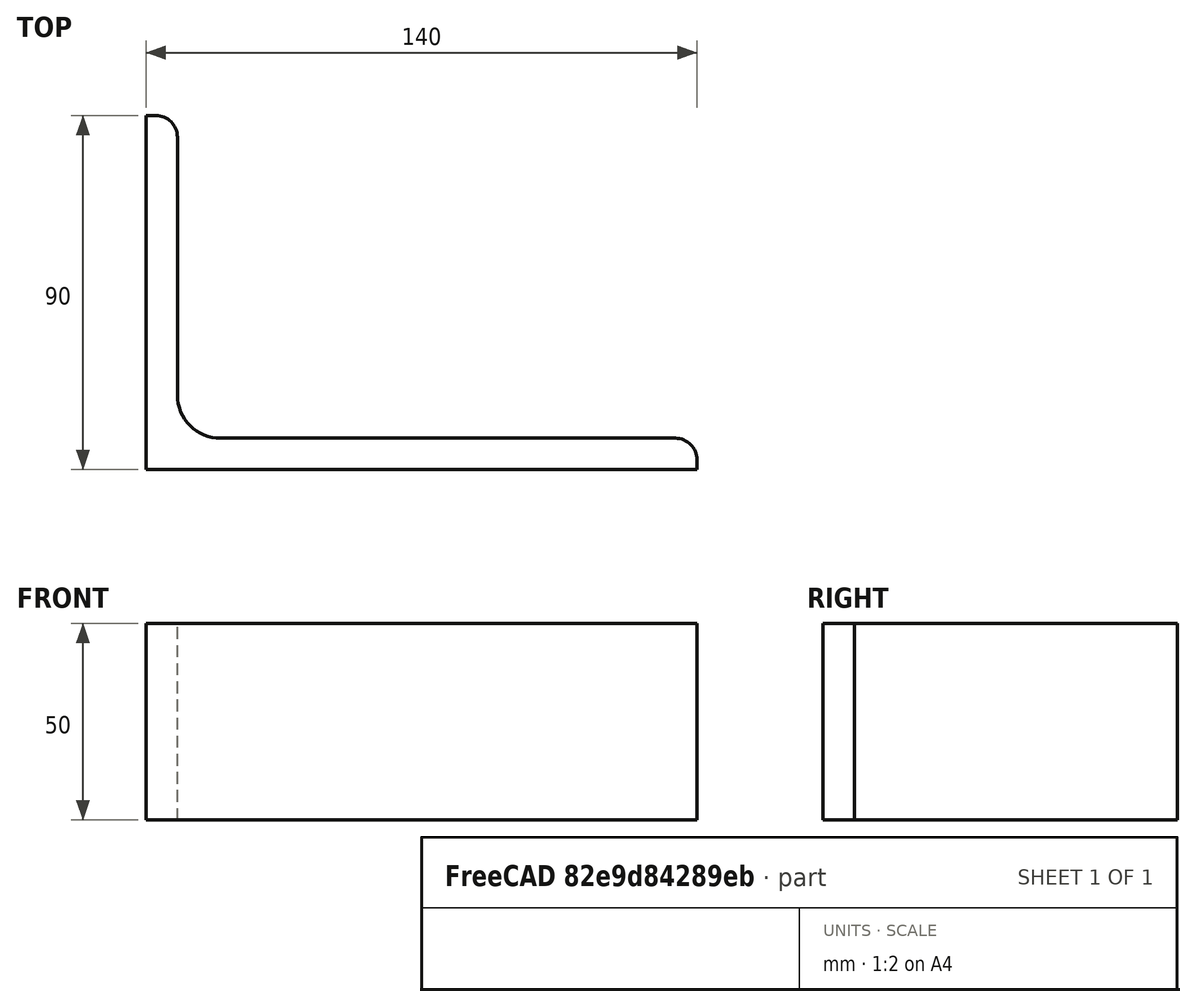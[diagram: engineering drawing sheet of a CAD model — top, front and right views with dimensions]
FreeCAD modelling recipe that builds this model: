
FCSTD DOCUMENT  (FreeCAD 0.15R4671 (Git))
Label: Angle Bar 140x90x8 EN10056 S235JR
License: All rights reserved
LicenseURL: http://en.wikipedia.org/wiki/All_rights_reserved
objects: Sketcher::SketchObject×1, Part::Extrusion×1
note: 2 computed .brp shape members not serialized (recipe doc carries the construction recipe); baked Part::Feature solids carry a one-line shape summary decoded from their .brp

FEATURE [Sketcher::SketchObject] Sketch
  sketch-geometry (9):
    g0: LineSegment StartX=0 StartY=0 StartZ=0 EndX=140 EndY=0 EndZ=0
    g1: LineSegment StartX=140 StartY=0 StartZ=0 EndX=140 EndY=2.5 EndZ=0
    g2: LineSegment StartX=134.5 StartY=8 StartZ=0 EndX=19 EndY=8 EndZ=0
    g3: LineSegment StartX=0 StartY=0 StartZ=0 EndX=0 EndY=90 EndZ=0
    g4: LineSegment StartX=0 StartY=90 StartZ=0 EndX=2.5 EndY=90 EndZ=0
    g5: LineSegment StartX=8 StartY=84.5 StartZ=0 EndX=8 EndY=19 EndZ=0
    g6: ArcOfCircle CenterX=19 CenterY=19 CenterZ=0 NormalX=0 NormalY=0 NormalZ=1 Radius=11 StartAngle=3.14159 EndAngle=4.71239
    g7: ArcOfCircle CenterX=2.5 CenterY=84.5 CenterZ=0 NormalX=0 NormalY=0 NormalZ=1 Radius=5.5 StartAngle=0 EndAngle=1.5708
    g8: ArcOfCircle CenterX=134.5 CenterY=2.5 CenterZ=0 NormalX=0 NormalY=0 NormalZ=1 Radius=5.5 StartAngle=0 EndAngle=1.5708
  constraints (23):
    c: Coincident(g0,g-1)
    c: Horizontal(g0)
    c: Coincident(g1,g0)
    c: Vertical(g1)
    c: Horizontal(g2)
    c: Coincident(g3,g-1)
    c: Vertical(g3)
    c: Coincident(g4,g3)
    c: Horizontal(g4)
    c: Vertical(g5)
    c: Tangent(g5,g6) = -1.5708
    c: Tangent(g2,g6) = 1.5708
    c: Tangent(g4,g7) = 1.5708
    c: Tangent(g5,g7) = 1.5708
    c: Tangent(g2,g8) = -1.5708
    c: Tangent(g1,g8) = -1.5708
    c: DistanceX(g0) = 140
    c: DistanceY(g3) = 90
    c: DistanceY(g0,g2) = 8
    c: DistanceX(g3,g5) = 8
    c: Radius(g6) = 11
    c: Radius(g8) = 5.5
    c: Radius(g7) = 5.5
FEATURE [Part::Extrusion] Extrude  label="Angle Bar 140x90x8 EN10056 S235JR"
  Base = -> Sketch
  Dir = (0,0,50)
  Solid = true
